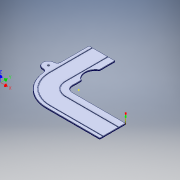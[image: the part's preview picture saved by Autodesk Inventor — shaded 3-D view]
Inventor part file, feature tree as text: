
AUTODESK INVENTOR PART (.ipt)
format: ipt  version: 2016 (Build 200138000, 138)  size: 242,176 bytes
history: native  units: in
note: dims shown in document units (in); Inventor stores cm internally (conversion verified against a paired STEP export)
features: sketch x1, other x1
ambient origin geometry x8: Origin, YZ Plane, XZ Plane, XY Plane, X Axis, Y Axis, Z Axis, Center Point
bodies: Solid1 (feature_tree)
feature tree (2):
  sketch  "Sketch1"
  other  "Cut-Extrude3"
